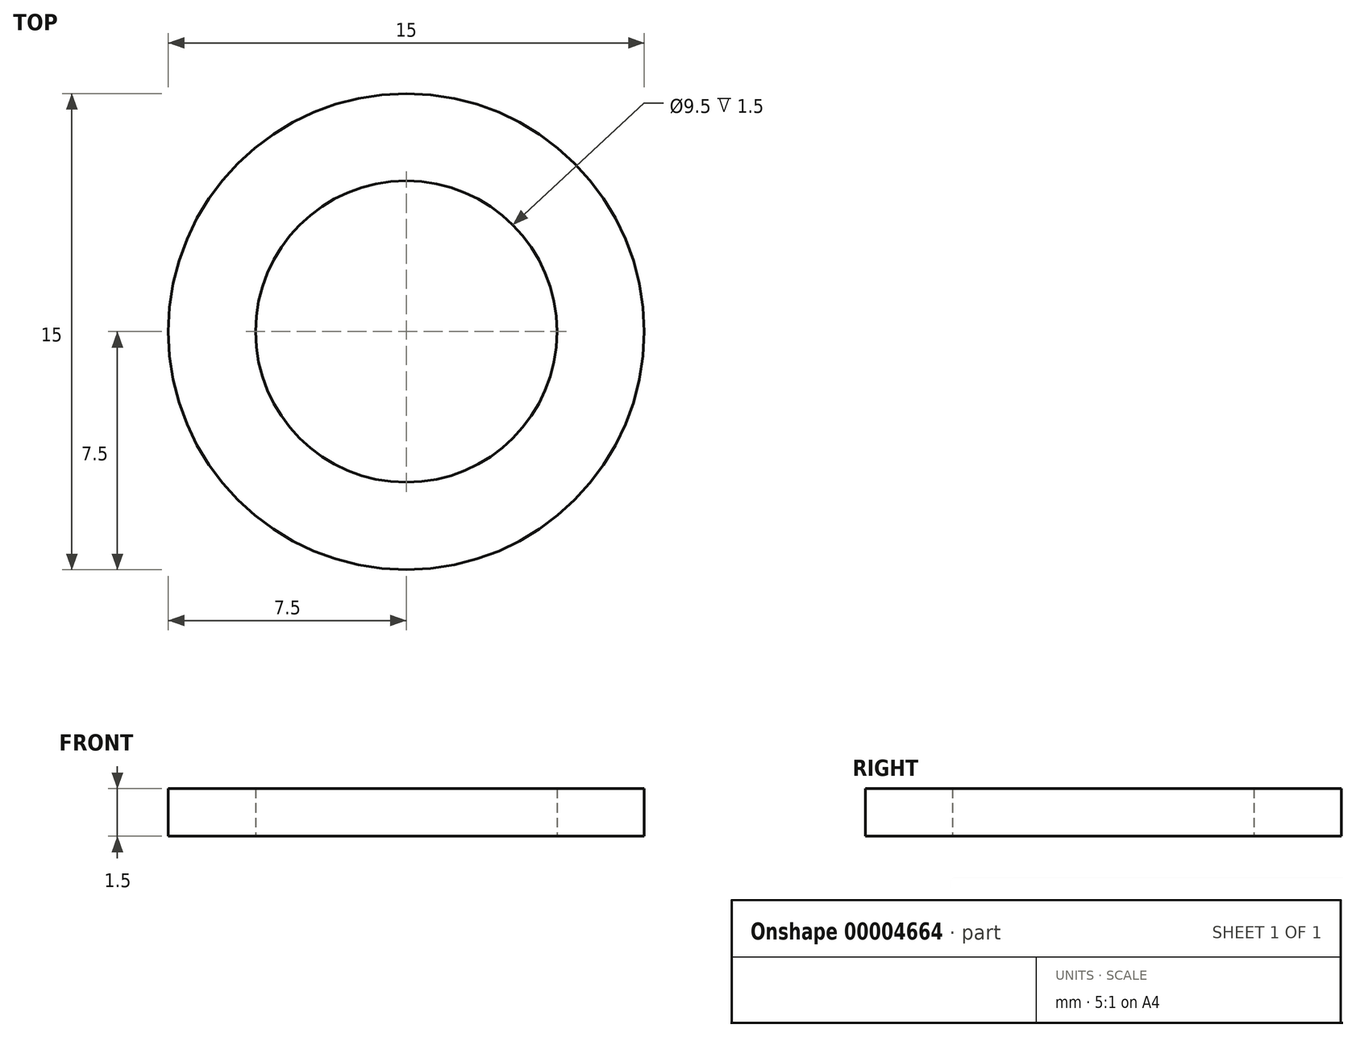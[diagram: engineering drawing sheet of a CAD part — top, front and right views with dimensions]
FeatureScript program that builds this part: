
annotation { "Feature Type Name" : "Feature", "Feature Type Description" : "" }
export const myFeature = defineFeature(function(context is Context, id is Id, definition is map)
    precondition{}
    {
        {
            var Q0;
            Q0=qCreatedBy(makeId("Top.planeOp"),FACE);
            var sketch = newSketch(context, id + "F0", { "sketchPlane" : qUnion([Q0])});
            skCircle(sketch, "E0", {"center": v(0, 0) * mm, "radius": 7.5 * mm});
            skCircle(sketch, "E1", {"center": v(0, 0) * mm, "radius": 4.75 * mm});
            skSolve(sketch);
        }
        {
            var Q0;
            Q0 = qSketchRegion(id + "F0", true);
            extrude(context, id + "F1", {"entities" : qUnion([Q0]), "depth" : 1.5 * mm});
        }
    });
